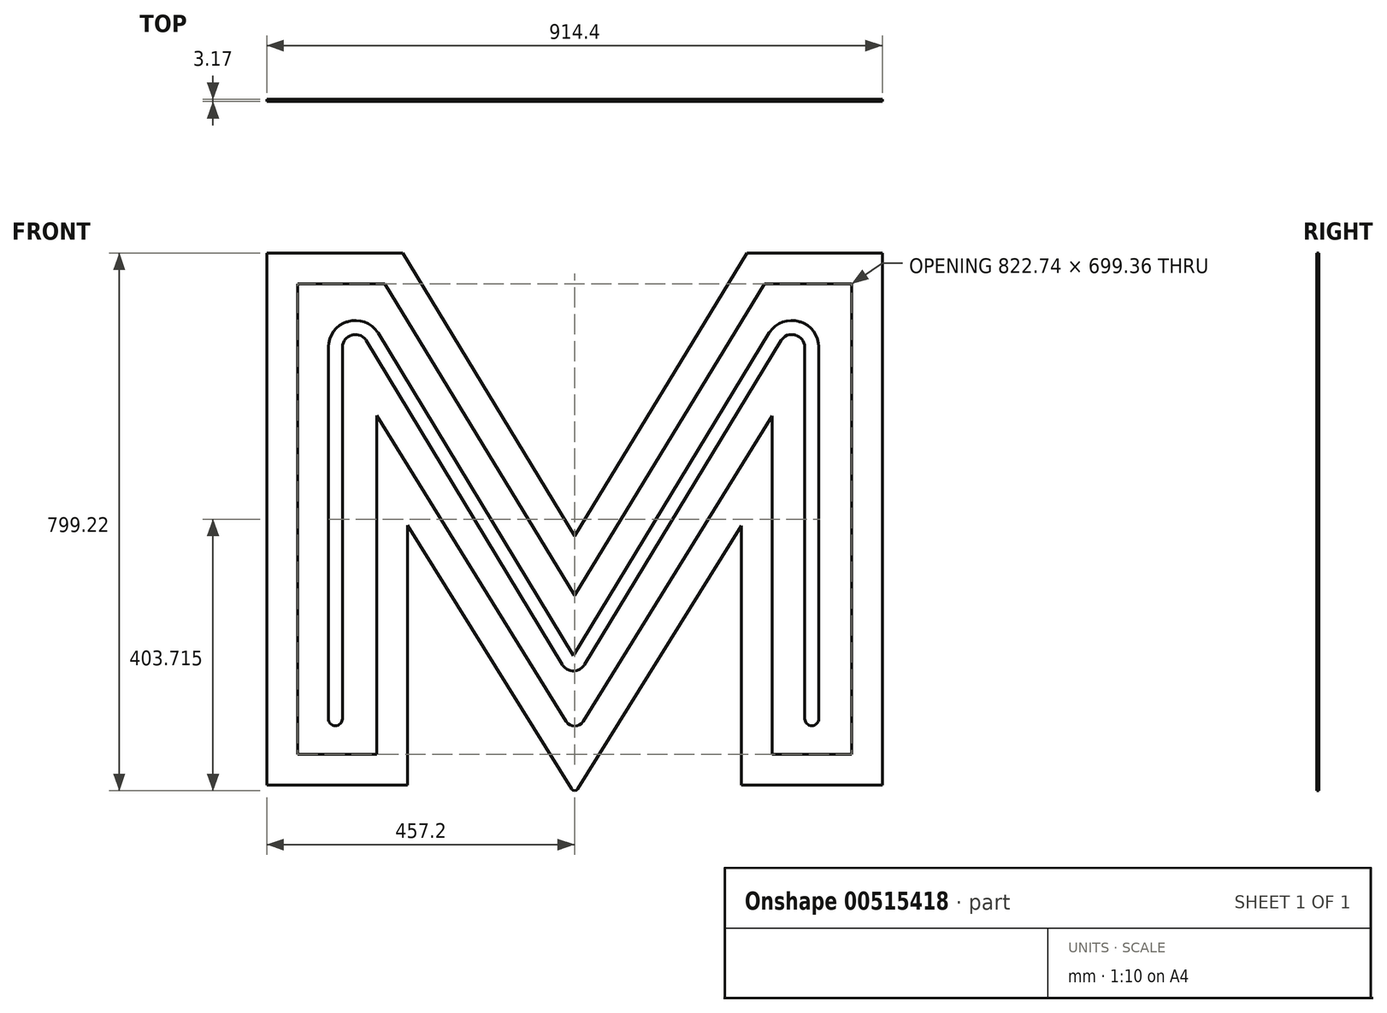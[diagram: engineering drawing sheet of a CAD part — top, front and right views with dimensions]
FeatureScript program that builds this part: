
annotation { "Feature Type Name" : "Feature", "Feature Type Description" : "" }
export const myFeature = defineFeature(function(context is Context, id is Id, definition is map)
    precondition{}
    {
        {
            var Q0;
            Q0=qCreatedBy(makeId("Front.planeOp"),FACE);
            var sketch = newSketch(context, id + "F0", { "sketchPlane" : qUnion([Q0])});
            skLineSegment(sketch, "E0", {"start": v(293.78, -345.57) * mm, "end": v(411.37, -345.57) * mm});
            skLineSegment(sketch, "E1", {"start": v(411.37, -345.57) * mm, "end": v(411.37, 353.78) * mm});
            skLineSegment(sketch, "E2", {"start": v(411.37, 353.78) * mm, "end": v(282.09, 353.78) * mm});
            skLineSegment(sketch, "E3", {"start": v(282.09, 353.78) * mm, "end": v(0, -108.92) * mm});
            skLineSegment(sketch, "E4", {"start": v(0, -108.92) * mm, "end": v(-281.9, 353.78) * mm});
            skLineSegment(sketch, "E5", {"start": v(-281.9, 353.78) * mm, "end": v(-411.37, 353.78) * mm});
            skLineSegment(sketch, "E6", {"start": v(-411.37, 353.78) * mm, "end": v(-411.37, -345.57) * mm});
            skLineSegment(sketch, "E7", {"start": v(-411.37, -345.57) * mm, "end": v(-293.78, -345.57) * mm});
            skLineSegment(sketch, "E8", {"start": v(-293.78, -345.57) * mm, "end": v(-293.78, 157.94) * mm});
            skLineSegment(sketch, "E9", {"start": v(-293.78, 157.94) * mm, "end": v(-12.54, -296.46) * mm});
            skLineSegment(sketch, "E10", {"start": v(-12.54, -296.46) * mm, "end": v(-12.03, -297.3) * mm});
            skLineSegment(sketch, "E11", {"start": v(-12.03, -297.3) * mm, "end": v(-10.03, -299.53) * mm});
            skLineSegment(sketch, "E12", {"start": v(-10.03, -299.53) * mm, "end": v(-6.98, -301.72) * mm});
            skLineSegment(sketch, "E13", {"start": v(-6.98, -301.72) * mm, "end": v(-3.56, -303.04) * mm});
            skLineSegment(sketch, "E14", {"start": v(-3.56, -303.04) * mm, "end": v(0.05, -303.48) * mm});
            skLineSegment(sketch, "E15", {"start": v(0.05, -303.48) * mm, "end": v(3.66, -303.04) * mm});
            skLineSegment(sketch, "E16", {"start": v(3.66, -303.04) * mm, "end": v(7.08, -301.72) * mm});
            skLineSegment(sketch, "E17", {"start": v(7.08, -301.72) * mm, "end": v(10.13, -299.53) * mm});
            skLineSegment(sketch, "E18", {"start": v(10.13, -299.53) * mm, "end": v(12.13, -297.3) * mm});
            skLineSegment(sketch, "E19", {"start": v(12.13, -297.3) * mm, "end": v(12.64, -296.46) * mm});
            skLineSegment(sketch, "E20", {"start": v(12.64, -296.46) * mm, "end": v(293.78, 157.62) * mm});
            skLineSegment(sketch, "E21", {"start": v(293.78, 157.62) * mm, "end": v(293.78, -345.57) * mm});
            skLineSegment(sketch, "E22", {"start": v(457.2, -391.4) * mm, "end": v(247.95, -391.4) * mm});
            skLineSegment(sketch, "E23", {"start": v(247.95, -391.4) * mm, "end": v(247.95, -5.62) * mm});
            skLineSegment(sketch, "E24", {"start": v(247.95, -5.62) * mm, "end": v(4.45, -397.12) * mm});
            skLineSegment(sketch, "E25", {"start": v(4.45, -397.12) * mm, "end": v(4.1, -397.68) * mm});
            skLineSegment(sketch, "E26", {"start": v(4.1, -397.68) * mm, "end": v(2.46, -399) * mm});
            skLineSegment(sketch, "E27", {"start": v(2.46, -399) * mm, "end": v(-0.05, -399.61) * mm});
            skLineSegment(sketch, "E28", {"start": v(-0.05, -399.61) * mm, "end": v(-2.55, -398.99) * mm});
            skLineSegment(sketch, "E29", {"start": v(-2.55, -398.99) * mm, "end": v(-4.2, -397.68) * mm});
            skLineSegment(sketch, "E30", {"start": v(-4.2, -397.68) * mm, "end": v(-4.54, -397.12) * mm});
            skLineSegment(sketch, "E31", {"start": v(-4.54, -397.12) * mm, "end": v(-247.95, -5.3) * mm});
            skLineSegment(sketch, "E32", {"start": v(-247.95, -5.3) * mm, "end": v(-247.95, -391.4) * mm});
            skLineSegment(sketch, "E33", {"start": v(-247.95, -391.4) * mm, "end": v(-457.2, -391.4) * mm});
            skLineSegment(sketch, "E34", {"start": v(-457.2, -391.4) * mm, "end": v(-457.2, 399.61) * mm});
            skLineSegment(sketch, "E35", {"start": v(-457.2, 399.61) * mm, "end": v(-255.12, 399.61) * mm});
            skLineSegment(sketch, "E36", {"start": v(-255.12, 399.61) * mm, "end": v(0.11, -20.77) * mm});
            skLineSegment(sketch, "E37", {"start": v(0.11, -20.77) * mm, "end": v(255.88, 399.61) * mm});
            skLineSegment(sketch, "E38", {"start": v(255.88, 399.61) * mm, "end": v(457.2, 399.61) * mm});
            skLineSegment(sketch, "E39", {"start": v(457.2, 399.61) * mm, "end": v(457.2, -391.4) * mm});
            skLineSegment(sketch, "E40", {"start": v(334.44, 297.53) * mm, "end": v(332.86, 298) * mm});
            skLineSegment(sketch, "E41", {"start": v(332.86, 298) * mm, "end": v(327.95, 298.97) * mm});
            skLineSegment(sketch, "E42", {"start": v(327.95, 298.97) * mm, "end": v(321.51, 299.34) * mm});
            skLineSegment(sketch, "E43", {"start": v(321.51, 299.34) * mm, "end": v(315.22, 298.69) * mm});
            skLineSegment(sketch, "E44", {"start": v(315.22, 298.69) * mm, "end": v(309.16, 297.04) * mm});
            skLineSegment(sketch, "E45", {"start": v(309.16, 297.04) * mm, "end": v(303.45, 294.42) * mm});
            skLineSegment(sketch, "E46", {"start": v(303.45, 294.42) * mm, "end": v(298.15, 290.88) * mm});
            skLineSegment(sketch, "E47", {"start": v(298.15, 290.88) * mm, "end": v(293.38, 286.44) * mm});
            skLineSegment(sketch, "E48", {"start": v(293.38, 286.44) * mm, "end": v(290.16, 282.54) * mm});
            skLineSegment(sketch, "E49", {"start": v(290.16, 282.54) * mm, "end": v(289.23, 281.15) * mm});
            skLineSegment(sketch, "E50", {"start": v(289.23, 281.15) * mm, "end": v(289.2, 281.1) * mm});
            skLineSegment(sketch, "E51", {"start": v(289.2, 281.1) * mm, "end": v(-1.57, -198.89) * mm});
            skLineSegment(sketch, "E52", {"start": v(-1.57, -198.89) * mm, "end": v(-292.22, 281.32) * mm});
            skLineSegment(sketch, "E53", {"start": v(-292.22, 281.32) * mm, "end": v(-292.29, 281.43) * mm});
            skLineSegment(sketch, "E54", {"start": v(-292.29, 281.43) * mm, "end": v(-293.21, 282.81) * mm});
            skLineSegment(sketch, "E55", {"start": v(-293.21, 282.81) * mm, "end": v(-296.4, 286.66) * mm});
            skLineSegment(sketch, "E56", {"start": v(-296.4, 286.66) * mm, "end": v(-301.14, 291.03) * mm});
            skLineSegment(sketch, "E57", {"start": v(-301.14, 291.03) * mm, "end": v(-306.4, 294.51) * mm});
            skLineSegment(sketch, "E58", {"start": v(-306.4, 294.51) * mm, "end": v(-312.1, 297.08) * mm});
            skLineSegment(sketch, "E59", {"start": v(-312.1, 297.08) * mm, "end": v(-318.13, 298.7) * mm});
            skLineSegment(sketch, "E60", {"start": v(-318.13, 298.7) * mm, "end": v(-324.4, 299.34) * mm});
            skLineSegment(sketch, "E61", {"start": v(-324.4, 299.34) * mm, "end": v(-330.84, 298.96) * mm});
            skLineSegment(sketch, "E62", {"start": v(-330.84, 298.96) * mm, "end": v(-335.75, 298) * mm});
            skLineSegment(sketch, "E63", {"start": v(-335.75, 298) * mm, "end": v(-337.33, 297.53) * mm});
            skLineSegment(sketch, "E64", {"start": v(-337.33, 297.53) * mm, "end": v(-338.92, 297.05) * mm});
            skLineSegment(sketch, "E65", {"start": v(-338.92, 297.05) * mm, "end": v(-343.52, 295.11) * mm});
            skLineSegment(sketch, "E66", {"start": v(-343.52, 295.11) * mm, "end": v(-349.08, 291.85) * mm});
            skLineSegment(sketch, "E67", {"start": v(-349.08, 291.85) * mm, "end": v(-353.95, 287.83) * mm});
            skLineSegment(sketch, "E68", {"start": v(-353.95, 287.83) * mm, "end": v(-358.06, 283.13) * mm});
            skLineSegment(sketch, "E69", {"start": v(-358.06, 283.13) * mm, "end": v(-361.36, 277.83) * mm});
            skLineSegment(sketch, "E70", {"start": v(-361.36, 277.83) * mm, "end": v(-363.8, 272) * mm});
            skLineSegment(sketch, "E71", {"start": v(-363.8, 272) * mm, "end": v(-365.3, 265.74) * mm});
            skLineSegment(sketch, "E72", {"start": v(-365.3, 265.74) * mm, "end": v(-365.81, 260.77) * mm});
            skLineSegment(sketch, "E73", {"start": v(-365.81, 260.77) * mm, "end": v(-365.81, 259.12) * mm});
            skLineSegment(sketch, "E74", {"start": v(-365.81, 259.12) * mm, "end": v(-365.81, -292.36) * mm});
            skLineSegment(sketch, "E75", {"start": v(-365.81, -292.36) * mm, "end": v(-365.81, -292.88) * mm});
            skLineSegment(sketch, "E76", {"start": v(-365.81, -292.88) * mm, "end": v(-365.6, -294.46) * mm});
            skLineSegment(sketch, "E77", {"start": v(-365.6, -294.46) * mm, "end": v(-364.99, -296.43) * mm});
            skLineSegment(sketch, "E78", {"start": v(-364.99, -296.43) * mm, "end": v(-364.02, -298.2) * mm});
            skLineSegment(sketch, "E79", {"start": v(-364.02, -298.2) * mm, "end": v(-362.75, -299.75) * mm});
            skLineSegment(sketch, "E80", {"start": v(-362.75, -299.75) * mm, "end": v(-361.2, -301.03) * mm});
            skLineSegment(sketch, "E81", {"start": v(-361.2, -301.03) * mm, "end": v(-359.42, -302) * mm});
            skLineSegment(sketch, "E82", {"start": v(-359.42, -302) * mm, "end": v(-357.46, -302.6) * mm});
            skLineSegment(sketch, "E83", {"start": v(-357.46, -302.6) * mm, "end": v(-355.88, -302.82) * mm});
            skLineSegment(sketch, "E84", {"start": v(-355.88, -302.82) * mm, "end": v(-355.35, -302.82) * mm});
            skLineSegment(sketch, "E85", {"start": v(-355.35, -302.82) * mm, "end": v(-354.83, -302.82) * mm});
            skLineSegment(sketch, "E86", {"start": v(-354.83, -302.82) * mm, "end": v(-353.25, -302.6) * mm});
            skLineSegment(sketch, "E87", {"start": v(-353.25, -302.6) * mm, "end": v(-351.28, -302) * mm});
            skLineSegment(sketch, "E88", {"start": v(-351.28, -302) * mm, "end": v(-349.5, -301.03) * mm});
            skLineSegment(sketch, "E89", {"start": v(-349.5, -301.03) * mm, "end": v(-347.96, -299.75) * mm});
            skLineSegment(sketch, "E90", {"start": v(-347.96, -299.75) * mm, "end": v(-346.68, -298.2) * mm});
            skLineSegment(sketch, "E91", {"start": v(-346.68, -298.2) * mm, "end": v(-345.72, -296.43) * mm});
            skLineSegment(sketch, "E92", {"start": v(-345.72, -296.43) * mm, "end": v(-345.1, -294.46) * mm});
            skLineSegment(sketch, "E93", {"start": v(-345.1, -294.46) * mm, "end": v(-344.9, -292.88) * mm});
            skLineSegment(sketch, "E94", {"start": v(-344.9, -292.88) * mm, "end": v(-344.9, -292.36) * mm});
            skLineSegment(sketch, "E95", {"start": v(-344.9, -292.36) * mm, "end": v(-344.9, 259.12) * mm});
            skLineSegment(sketch, "E96", {"start": v(-344.9, 259.12) * mm, "end": v(-344.9, 260.05) * mm});
            skLineSegment(sketch, "E97", {"start": v(-344.9, 260.05) * mm, "end": v(-344.58, 262.85) * mm});
            skLineSegment(sketch, "E98", {"start": v(-344.58, 262.85) * mm, "end": v(-343.69, 266.15) * mm});
            skLineSegment(sketch, "E99", {"start": v(-343.69, 266.15) * mm, "end": v(-342.32, 269.03) * mm});
            skLineSegment(sketch, "E100", {"start": v(-342.32, 269.03) * mm, "end": v(-340.55, 271.5) * mm});
            skLineSegment(sketch, "E101", {"start": v(-340.55, 271.5) * mm, "end": v(-338.47, 273.58) * mm});
            skLineSegment(sketch, "E102", {"start": v(-338.47, 273.58) * mm, "end": v(-336.17, 275.27) * mm});
            skLineSegment(sketch, "E103", {"start": v(-336.17, 275.27) * mm, "end": v(-333.74, 276.57) * mm});
            skLineSegment(sketch, "E104", {"start": v(-333.74, 276.57) * mm, "end": v(-331.9, 277.31) * mm});
            skLineSegment(sketch, "E105", {"start": v(-331.9, 277.31) * mm, "end": v(-331.27, 277.5) * mm});
            skLineSegment(sketch, "E106", {"start": v(-331.27, 277.5) * mm, "end": v(-330.63, 277.7) * mm});
            skLineSegment(sketch, "E107", {"start": v(-330.63, 277.7) * mm, "end": v(-328.69, 278.1) * mm});
            skLineSegment(sketch, "E108", {"start": v(-328.69, 278.1) * mm, "end": v(-325.95, 278.38) * mm});
            skLineSegment(sketch, "E109", {"start": v(-325.95, 278.38) * mm, "end": v(-323.11, 278.27) * mm});
            skLineSegment(sketch, "E110", {"start": v(-323.11, 278.27) * mm, "end": v(-320.25, 277.73) * mm});
            skLineSegment(sketch, "E111", {"start": v(-320.25, 277.73) * mm, "end": v(-317.43, 276.7) * mm});
            skLineSegment(sketch, "E112", {"start": v(-317.43, 276.7) * mm, "end": v(-314.72, 275.14) * mm});
            skLineSegment(sketch, "E113", {"start": v(-314.72, 275.14) * mm, "end": v(-312.19, 272.96) * mm});
            skLineSegment(sketch, "E114", {"start": v(-312.19, 272.96) * mm, "end": v(-310.4, 270.9) * mm});
            skLineSegment(sketch, "E115", {"start": v(-310.4, 270.9) * mm, "end": v(-309.9, 270.14) * mm});
            skLineSegment(sketch, "E116", {"start": v(-309.9, 270.14) * mm, "end": v(-18.05, -212.06) * mm});
            skLineSegment(sketch, "E117", {"start": v(-18.05, -212.06) * mm, "end": v(-17.41, -213.12) * mm});
            skLineSegment(sketch, "E118", {"start": v(-17.41, -213.12) * mm, "end": v(-14.95, -215.96) * mm});
            skLineSegment(sketch, "E119", {"start": v(-14.95, -215.96) * mm, "end": v(-11.04, -218.88) * mm});
            skLineSegment(sketch, "E120", {"start": v(-11.04, -218.88) * mm, "end": v(-6.52, -220.7) * mm});
            skLineSegment(sketch, "E121", {"start": v(-6.52, -220.7) * mm, "end": v(-2.81, -221.34) * mm});
            skLineSegment(sketch, "E122", {"start": v(-2.81, -221.34) * mm, "end": v(-1.57, -221.34) * mm});
            skLineSegment(sketch, "E123", {"start": v(-1.57, -221.34) * mm, "end": v(-0.34, -221.34) * mm});
            skLineSegment(sketch, "E124", {"start": v(-0.34, -221.34) * mm, "end": v(3.37, -220.7) * mm});
            skLineSegment(sketch, "E125", {"start": v(3.37, -220.7) * mm, "end": v(7.89, -218.88) * mm});
            skLineSegment(sketch, "E126", {"start": v(7.89, -218.88) * mm, "end": v(11.8, -215.97) * mm});
            skLineSegment(sketch, "E127", {"start": v(11.8, -215.97) * mm, "end": v(14.27, -213.12) * mm});
            skLineSegment(sketch, "E128", {"start": v(14.27, -213.12) * mm, "end": v(14.9, -212.07) * mm});
            skLineSegment(sketch, "E129", {"start": v(14.9, -212.07) * mm, "end": v(306.85, 269.86) * mm});
            skLineSegment(sketch, "E130", {"start": v(306.85, 269.86) * mm, "end": v(307.48, 270.8) * mm});
            skLineSegment(sketch, "E131", {"start": v(307.48, 270.8) * mm, "end": v(309.74, 273.36) * mm});
            skLineSegment(sketch, "E132", {"start": v(309.74, 273.36) * mm, "end": v(312.84, 275.8) * mm});
            skLineSegment(sketch, "E133", {"start": v(312.84, 275.8) * mm, "end": v(316.02, 277.33) * mm});
            skLineSegment(sketch, "E134", {"start": v(316.02, 277.33) * mm, "end": v(319.14, 278.14) * mm});
            skLineSegment(sketch, "E135", {"start": v(319.14, 278.14) * mm, "end": v(322.08, 278.4) * mm});
            skLineSegment(sketch, "E136", {"start": v(322.08, 278.4) * mm, "end": v(324.68, 278.26) * mm});
            skLineSegment(sketch, "E137", {"start": v(324.68, 278.26) * mm, "end": v(326.82, 277.9) * mm});
            skLineSegment(sketch, "E138", {"start": v(326.82, 277.9) * mm, "end": v(327.98, 277.63) * mm});
            skLineSegment(sketch, "E139", {"start": v(327.98, 277.63) * mm, "end": v(328.36, 277.51) * mm});
            skLineSegment(sketch, "E140", {"start": v(328.36, 277.51) * mm, "end": v(329, 277.32) * mm});
            skLineSegment(sketch, "E141", {"start": v(329, 277.32) * mm, "end": v(330.84, 276.58) * mm});
            skLineSegment(sketch, "E142", {"start": v(330.84, 276.58) * mm, "end": v(333.27, 275.27) * mm});
            skLineSegment(sketch, "E143", {"start": v(333.27, 275.27) * mm, "end": v(335.57, 273.58) * mm});
            skLineSegment(sketch, "E144", {"start": v(335.57, 273.58) * mm, "end": v(337.65, 271.5) * mm});
            skLineSegment(sketch, "E145", {"start": v(337.65, 271.5) * mm, "end": v(339.42, 269.03) * mm});
            skLineSegment(sketch, "E146", {"start": v(339.42, 269.03) * mm, "end": v(340.79, 266.14) * mm});
            skLineSegment(sketch, "E147", {"start": v(340.79, 266.14) * mm, "end": v(341.68, 262.85) * mm});
            skLineSegment(sketch, "E148", {"start": v(341.68, 262.85) * mm, "end": v(342, 260.05) * mm});
            skLineSegment(sketch, "E149", {"start": v(342, 260.05) * mm, "end": v(342, 259.12) * mm});
            skLineSegment(sketch, "E150", {"start": v(342, 259.12) * mm, "end": v(342, -292.36) * mm});
            skLineSegment(sketch, "E151", {"start": v(342, -292.36) * mm, "end": v(342, -292.88) * mm});
            skLineSegment(sketch, "E152", {"start": v(342, -292.88) * mm, "end": v(342.2, -294.46) * mm});
            skLineSegment(sketch, "E153", {"start": v(342.2, -294.46) * mm, "end": v(342.82, -296.43) * mm});
            skLineSegment(sketch, "E154", {"start": v(342.82, -296.43) * mm, "end": v(343.79, -298.2) * mm});
            skLineSegment(sketch, "E155", {"start": v(343.79, -298.2) * mm, "end": v(345.06, -299.75) * mm});
            skLineSegment(sketch, "E156", {"start": v(345.06, -299.75) * mm, "end": v(346.61, -301.03) * mm});
            skLineSegment(sketch, "E157", {"start": v(346.61, -301.03) * mm, "end": v(348.39, -302) * mm});
            skLineSegment(sketch, "E158", {"start": v(348.39, -302) * mm, "end": v(350.35, -302.6) * mm});
            skLineSegment(sketch, "E159", {"start": v(350.35, -302.6) * mm, "end": v(351.93, -302.82) * mm});
            skLineSegment(sketch, "E160", {"start": v(351.93, -302.82) * mm, "end": v(352.46, -302.82) * mm});
            skLineSegment(sketch, "E161", {"start": v(352.46, -302.82) * mm, "end": v(352.98, -302.82) * mm});
            skLineSegment(sketch, "E162", {"start": v(352.98, -302.82) * mm, "end": v(354.56, -302.6) * mm});
            skLineSegment(sketch, "E163", {"start": v(354.56, -302.6) * mm, "end": v(356.53, -302) * mm});
            skLineSegment(sketch, "E164", {"start": v(356.53, -302) * mm, "end": v(358.3, -301.03) * mm});
            skLineSegment(sketch, "E165", {"start": v(358.3, -301.03) * mm, "end": v(359.85, -299.75) * mm});
            skLineSegment(sketch, "E166", {"start": v(359.85, -299.75) * mm, "end": v(361.13, -298.2) * mm});
            skLineSegment(sketch, "E167", {"start": v(361.13, -298.2) * mm, "end": v(362.1, -296.43) * mm});
            skLineSegment(sketch, "E168", {"start": v(362.1, -296.43) * mm, "end": v(362.7, -294.46) * mm});
            skLineSegment(sketch, "E169", {"start": v(362.7, -294.46) * mm, "end": v(362.92, -292.88) * mm});
            skLineSegment(sketch, "E170", {"start": v(362.92, -292.88) * mm, "end": v(362.92, -292.36) * mm});
            skLineSegment(sketch, "E171", {"start": v(362.92, -292.36) * mm, "end": v(362.92, 259.12) * mm});
            skLineSegment(sketch, "E172", {"start": v(362.92, 259.12) * mm, "end": v(362.92, 260.78) * mm});
            skLineSegment(sketch, "E173", {"start": v(362.92, 260.78) * mm, "end": v(362.4, 265.75) * mm});
            skLineSegment(sketch, "E174", {"start": v(362.4, 265.75) * mm, "end": v(360.9, 272) * mm});
            skLineSegment(sketch, "E175", {"start": v(360.9, 272) * mm, "end": v(358.47, 277.83) * mm});
            skLineSegment(sketch, "E176", {"start": v(358.47, 277.83) * mm, "end": v(355.17, 283.14) * mm});
            skLineSegment(sketch, "E177", {"start": v(355.17, 283.14) * mm, "end": v(351.05, 287.84) * mm});
            skLineSegment(sketch, "E178", {"start": v(351.05, 287.84) * mm, "end": v(346.18, 291.85) * mm});
            skLineSegment(sketch, "E179", {"start": v(346.18, 291.85) * mm, "end": v(340.63, 295.11) * mm});
            skLineSegment(sketch, "E180", {"start": v(340.63, 295.11) * mm, "end": v(336.02, 297.05) * mm});
            skLineSegment(sketch, "E181", {"start": v(336.02, 297.05) * mm, "end": v(334.44, 297.53) * mm});
            skSolve(sketch);
        }
        {
            var Q0;
            Q0 = qSketchRegion(id + "F0", true);
            var Q1;
            Q1=makeQuery(id+"F0.imprint","IMPRINT",FACE,{"disambiguationData":[TD([[makeQuery(id+"F0.imprint","IMPRINT",EDGE,{"derivedFrom":sQuery(id+"F0.wireOp",EDGE,"E40")}),1.0]])]});
            extrude(context, id + "F1", {"entities" : qUnion([Q0, Q1]), "depth" : 3.17 * mm, "offsetDistance" : 25.4 * mm});
        }
    });
